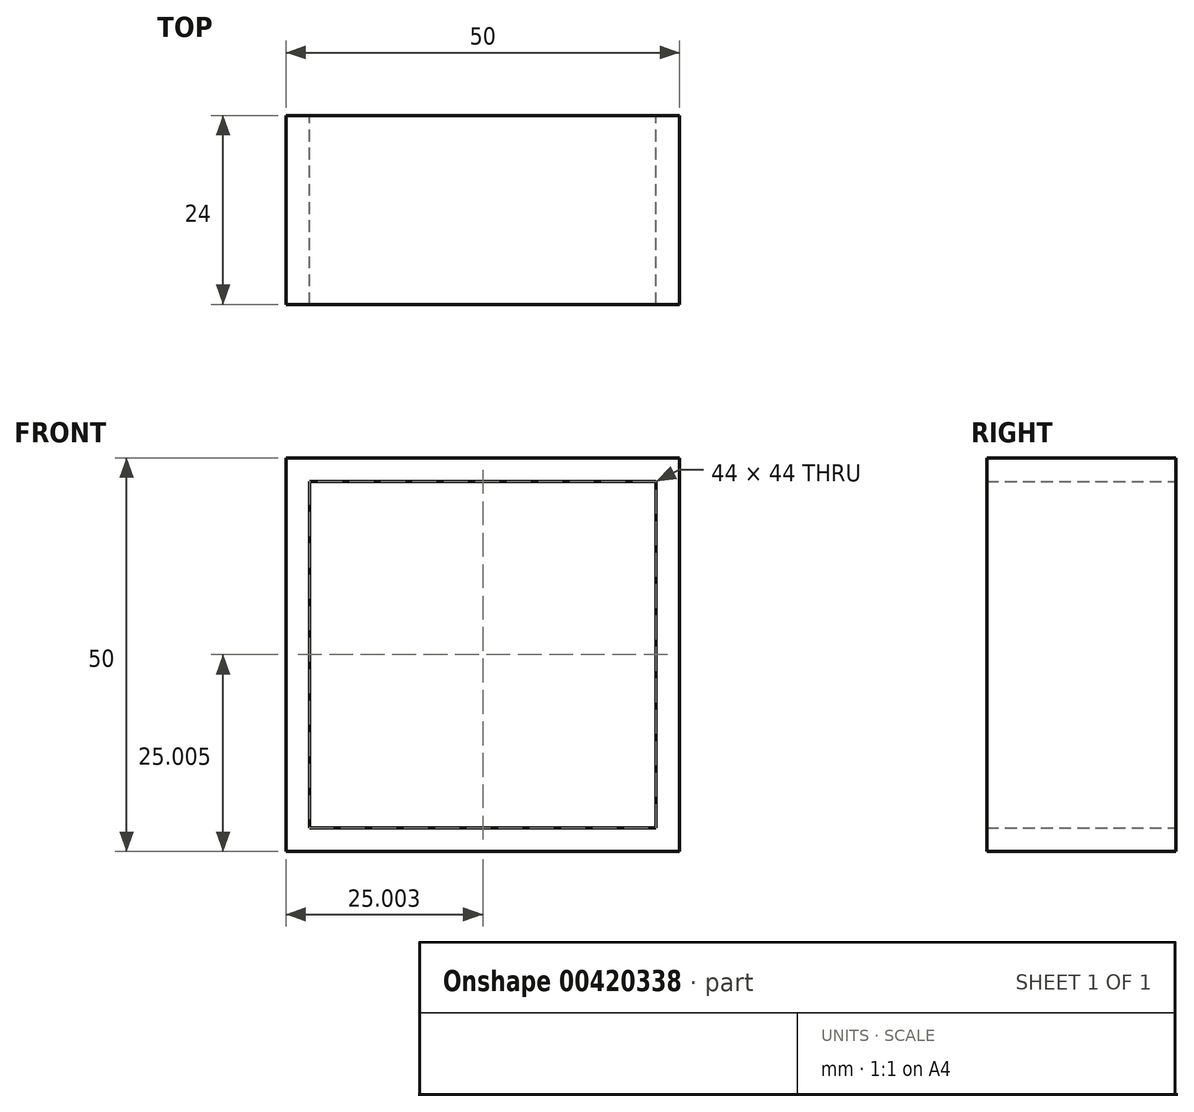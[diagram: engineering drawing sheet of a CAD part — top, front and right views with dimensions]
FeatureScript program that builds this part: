
annotation { "Feature Type Name" : "Feature", "Feature Type Description" : "" }
export const myFeature = defineFeature(function(context is Context, id is Id, definition is map)
    precondition{}
    {
        {
            var Q0;
            Q0=qCreatedBy(makeId("Front.planeOp"),FACE);
            var sketch = newSketch(context, id + "F0", { "sketchPlane" : qUnion([Q0])});
            skLineSegment(sketch, "E0.bottom", {"start": v(-20.92, 25.5) * mm, "end": v(29.08, 25.5) * mm});
            skLineSegment(sketch, "E0.top", {"start": v(-20.92, -24.5) * mm, "end": v(29.08, -24.5) * mm});
            skLineSegment(sketch, "E0.left", {"start": v(-20.92, 25.5) * mm, "end": v(-20.92, -24.5) * mm});
            skLineSegment(sketch, "E0.right", {"start": v(29.08, 25.5) * mm, "end": v(29.08, -24.5) * mm});
            skLineSegment(sketch, "E1.bottom", {"start": v(-17.92, 22.5) * mm, "end": v(26.08, 22.5) * mm});
            skLineSegment(sketch, "E1.top", {"start": v(-17.92, -21.5) * mm, "end": v(26.08, -21.5) * mm});
            skLineSegment(sketch, "E1.left", {"start": v(-17.92, 22.5) * mm, "end": v(-17.92, -21.5) * mm});
            skLineSegment(sketch, "E1.right", {"start": v(26.08, 22.5) * mm, "end": v(26.08, -21.5) * mm});
            skSolve(sketch);
        }
        {
            var Q0;
            Q0=qSketchRegion(id+"F0",true);
            extrude(context, id + "F1", {"entities" : qUnion([Q0]), "depth" : 24 * mm});
        }
    });
